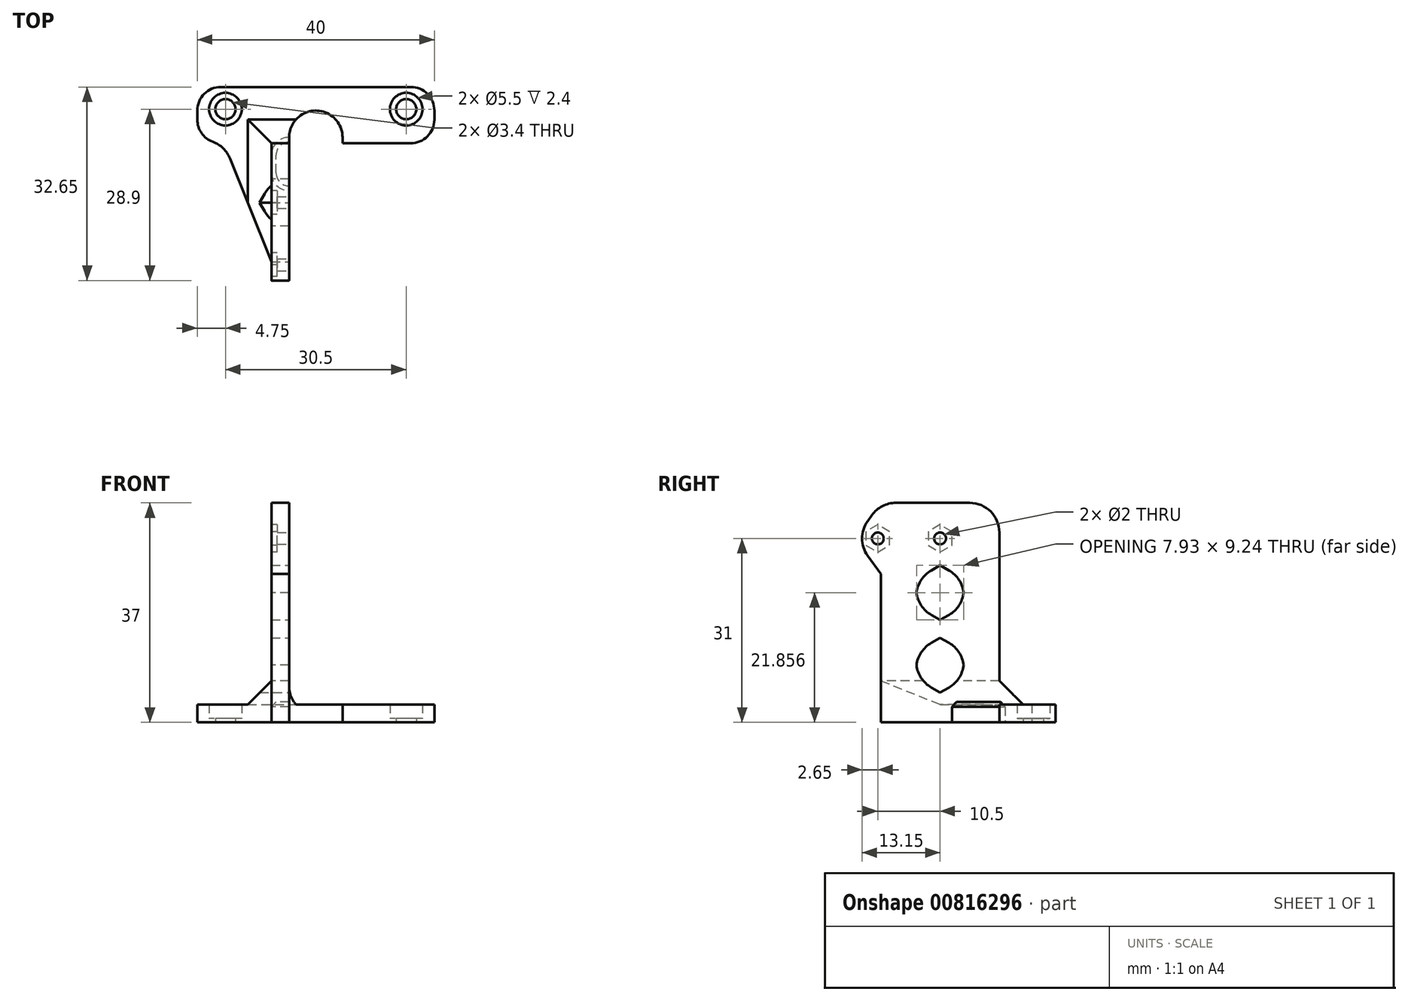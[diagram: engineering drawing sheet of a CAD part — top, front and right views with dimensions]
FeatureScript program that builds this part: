
annotation { "Feature Type Name" : "Feature", "Feature Type Description" : "" }
export const myFeature = defineFeature(function(context is Context, id is Id, definition is map)
    precondition{}
    {
        {
            var Q0;
            Q0=qCreatedBy(makeId("Top.planeOp"),FACE);
            var sketch = newSketch(context, id + "F0", { "sketchPlane" : qUnion([Q0])});
            skLineSegment(sketch, "E0.bottom", {"start": v(-20, 14.75) * mm, "end": v(20, 14.75) * mm});
            skLineSegment(sketch, "E0.top", {"start": v(-20, -14.75) * mm, "end": v(20, -14.75) * mm});
            skLineSegment(sketch, "E0.left", {"start": v(-20, 14.75) * mm, "end": v(-20, -14.75) * mm});
            skLineSegment(sketch, "E0.right", {"start": v(20, 14.75) * mm, "end": v(20, -14.75) * mm});
            skCircle(sketch, "E1", {"center": v(-15.25, 11) * mm, "radius": 2.75 * mm});
            skCircle(sketch, "E2", {"center": v(15.25, 11) * mm, "radius": 2.75 * mm});
            skLineSegment(sketch, "E3", {"start": v(-15.25, 11) * mm, "end": v(15.25, 11) * mm, "construction": true});
            skPoint(sketch, "E4", {"position": v(0, 11) * mm});
            skPoint(sketch, "E5", {"position": v(0, 14.75) * mm});
            skPoint(sketch, "E6", {"position": v(-20, 0) * mm});
            skCircle(sketch, "E7", {"center": v(0, 6.25) * mm, "radius": 4.5 * mm});
            skLineSegment(sketch, "E8", {"start": v(4.5, 6.25) * mm, "end": v(4.5, -14.75) * mm});
            skLineSegment(sketch, "E9", {"start": v(-4.5, 6.25) * mm, "end": v(-4.5, -14.75) * mm});
            skLineSegment(sketch, "E10", {"start": v(-4.5, 5.25) * mm, "end": v(-7.5, 5.25) * mm});
            skLineSegment(sketch, "E11", {"start": v(-7.5, 5.25) * mm, "end": v(-7.5, -14.75) * mm});
            skLineSegment(sketch, "E12", {"start": v(4.5, 5.25) * mm, "end": v(20, 5.25) * mm});
            skLineSegment(sketch, "E13", {"start": v(-7.5, 5.25) * mm, "end": v(-20, 5.25) * mm});
            skCircle(sketch, "E14", {"center": v(-15.25, 11) * mm, "radius": 1.7 * mm});
            skCircle(sketch, "E15", {"center": v(15.25, 11) * mm, "radius": 1.7 * mm});
            skPoint(sketch, "E16", {"position": v(0, 10.75) * mm});
            skPoint(sketch, "E17", {"position": v(15.25, 13.75) * mm});
            skSolve(sketch);
        }
        {
            var Q0;
            {var subQ4=sQuery(id+"F0.wireOp",EDGE,"E10");Q0=makeQuery(id+"F0.imprint","IMPRINT",FACE,{"disambiguationData":[TD([[makeQuery(id+"F0.imprint","IMPRINT",EDGE,{"derivedFrom":subQ4}),1.0]])]});}
            var Q1;
            {var subQ7=sQuery(id+"F0.wireOp",EDGE,"E0.bottom");Q1=makeQuery(id+"F0.imprint","IMPRINT",FACE,{"disambiguationData":[TD([[makeQuery(id+"F0.imprint","IMPRINT",EDGE,{"derivedFrom":subQ7}),-1.0]])]});}
            extrude(context, id + "F1", {"entities" : qUnion([Q0, Q1]), "depth" : 3 * mm, "offsetDistance" : 25 * mm});
        }
        {
            var Q0;
            {var subQ4=sQuery(id+"F0.wireOp",EDGE,"E10");Q0=makeQuery(id+"F0.imprint","IMPRINT",FACE,{"disambiguationData":[TD([[makeQuery(id+"F0.imprint","IMPRINT",EDGE,{"derivedFrom":subQ4}),1.0]])]});}
            extrude(context, id + "F2", {"entities" : qUnion([Q0]), "operationType" : NewBodyOperationType.ADD, "flatOperationType" : FlatOperationType.REMOVE, "depth" : (46 - 9) * mm, "offsetDistance" : 25 * mm, "domain" : OperationDomain.MODEL});
        }
        {
            var Q0;
            Q0=makeQuery(id+"F1.opExtrude","SWEPT_EDGE",EDGE,{"disambiguationData":[OSD([sQuery(id+"F0.wireOp",EDGE,"E0.right"),sQuery(id+"F0.wireOp",EDGE,"E12")])]});
            var Q1;
            Q1=makeQuery(id+"F1.opExtrude","SWEPT_EDGE",EDGE,{"disambiguationData":[OSD([sQuery(id+"F0.wireOp",EDGE,"E0.bottom"),sQuery(id+"F0.wireOp",EDGE,"E0.right")])]});
            var Q2;
            Q2=makeQuery(id+"F1.opExtrude","SWEPT_EDGE",EDGE,{"disambiguationData":[OSD([sQuery(id+"F0.wireOp",EDGE,"E0.left"),sQuery(id+"F0.wireOp",EDGE,"E13")])]});
            var Q3;
            Q3=makeQuery(id+"F1.opExtrude","SWEPT_EDGE",EDGE,{"disambiguationData":[OSD([sQuery(id+"F0.wireOp",EDGE,"E0.bottom"),sQuery(id+"F0.wireOp",EDGE,"E0.left")])]});
            fillet(context, id + "F3", {"entities" : qUnion([Q0, Q1, Q2, Q3]), "radius" : 4 * mm, "tangentPropagation" : true, "allowEdgeOverflow" : false});
        }
        {
            var Q0;
            Q0=makeQuery(id+"F1.opExtrude","SWEPT_EDGE",EDGE,{"disambiguationData":[OSD([sQuery(id+"F0.wireOp",EDGE,"E10"),sQuery(id+"F0.wireOp",EDGE,"E11"),sQuery(id+"F0.wireOp",EDGE,"E13")])]});
            chamfer(context, id + "F4", {"entities" : qUnion([Q0]), "chamferType" : ChamferType.TWO_OFFSETS, "width1" : 20 * mm, "oppositeDirection" : false, "width2" : 8 * mm, "tangentPropagation" : true});
        }
        {
            var Q0;
            {var subQ0=sQuery(id+"F0.wireOp",EDGE,"E13");Q0=makeQuery(id+"F4.opChamfer","BLEND_EDGE",EDGE,{"blendedFrom":[makeQuery(id+"F1.opExtrude","SWEPT_EDGE",EDGE,{"disambiguationData":[OSD([sQuery(id+"F0.wireOp",EDGE,"E10"),sQuery(id+"F0.wireOp",EDGE,"E11"),subQ0])]}),makeQuery(id+"F1.opExtrude","SWEPT_FACE",FACE,{"disambiguationData":[OSD([subQ0])]})],"blendedInto":[makeQuery(id+"F1.opExtrude","SWEPT_FACE",FACE,{"disambiguationData":[OSD([subQ0])]})]});}
            fillet(context, id + "F5", {"entities" : qUnion([Q0]), "radius" : 5 * mm, "tangentPropagation" : true, "allowEdgeOverflow" : false});
        }
        {
            var Q0;
            Q0=makeQuery(id+"F4.opChamfer","TWEAK_EDGE",EDGE,{"derivedFrom":[makeQuery(id+"F1.opExtrude","CAP_VERTEX",VERTEX,{"disambiguationData":[OSD([sQuery(id+"F0.wireOp",EDGE,"E10"),sQuery(id+"F0.wireOp",EDGE,"E11"),sQuery(id+"F0.wireOp",EDGE,"E13")])],"isStart":false})]});
            chamfer(context, id + "F6", {"entities" : qUnion([Q0]), "width" : 4 * mm, "tangentPropagation" : true});
        }
        {
            var Q0;
            {var subQ0=sQuery(id+"F0.wireOp",EDGE,"E9");Q0=makeQuery(id+"F2.boolean.opBoolean","MERGE",FACE,{"derivedFrom":[makeQuery(id+"F1.opExtrude","SWEPT_FACE",FACE,{"disambiguationData":[OSD([subQ0])]}),makeQuery(id+"F2.opExtrude","SWEPT_FACE",FACE,{"disambiguationData":[OSD([subQ0])]})]});}
            var sketch = newSketch(context, id + "F7", { "sketchPlane" : qUnion([Q0])});
            skCircle(sketch, "E18.cCircle", {"center": v(-4.75, 9.62) * mm, "radius": 4 * mm, "construction": true});
            skLineSegment(sketch, "E18.0", {"start": v(-8.75, 7.3) * mm, "end": v(-8.75, 11.93) * mm});
            skLineSegment(sketch, "E18.1", {"start": v(-8.75, 11.93) * mm, "end": v(-4.75, 14.24) * mm});
            skLineSegment(sketch, "E18.2", {"start": v(-4.75, 14.24) * mm, "end": v(-0.75, 11.93) * mm});
            skLineSegment(sketch, "E18.3", {"start": v(-0.75, 11.93) * mm, "end": v(-0.75, 7.3) * mm});
            skLineSegment(sketch, "E18.4", {"start": v(-0.75, 7.3) * mm, "end": v(-4.75, 5) * mm});
            skLineSegment(sketch, "E18.5", {"start": v(-4.75, 5) * mm, "end": v(-8.75, 7.3) * mm});
            skPoint(sketch, "E18.0.midPoint", {"position": v(-8.75, 9.62) * mm});
            skPoint(sketch, "E19", {"position": v(-4.75, 37) * mm});
            skCircle(sketch, "E20", {"center": v(-15.25, 31) * mm, "radius": 1 * mm});
            skCircle(sketch, "E21", {"center": v(-4.75, 31) * mm, "radius": 1 * mm});
            skLineSegment(sketch, "E22", {"start": v(-14.75, 25) * mm, "end": v(-19.05, 31) * mm});
            skLineSegment(sketch, "E23", {"start": v(-19.05, 31) * mm, "end": v(-14.75, 37) * mm});
            skCircle(sketch, "E24.cCircle", {"center": v(-4.75, 21.86) * mm, "radius": 4 * mm, "construction": true});
            skLineSegment(sketch, "E24.0", {"start": v(-8.75, 19.55) * mm, "end": v(-8.75, 24.17) * mm});
            skLineSegment(sketch, "E24.1", {"start": v(-8.75, 24.17) * mm, "end": v(-4.75, 26.48) * mm});
            skLineSegment(sketch, "E24.2", {"start": v(-4.75, 26.48) * mm, "end": v(-0.75, 24.17) * mm});
            skLineSegment(sketch, "E24.3", {"start": v(-0.75, 24.17) * mm, "end": v(-0.75, 19.55) * mm});
            skLineSegment(sketch, "E24.4", {"start": v(-0.75, 19.55) * mm, "end": v(-4.75, 17.24) * mm});
            skLineSegment(sketch, "E24.5", {"start": v(-4.75, 17.24) * mm, "end": v(-8.75, 19.55) * mm});
            skPoint(sketch, "E24.0.midPoint", {"position": v(-8.75, 21.86) * mm});
            skSolve(sketch);
        }
        {
            var Q0;
            Q0=makeQuery(id+"F7.imprint","IMPRINT",FACE,{"disambiguationData":[TD([[makeQuery(id+"F7.imprint","IMPRINT",EDGE,{"derivedFrom":sQuery(id+"F7.wireOp",EDGE,"E24.0")}),-1.0]])]});
            var Q1;
            {var subQ0=sQuery(id+"F7.wireOp",EDGE,"E20");var subQ1=sQuery(id+"F0.wireOp",EDGE,"E9");var subQ2=sQuery(id+"F0.wireOp",EDGE,"E0.top");var subQ3=makeQuery(id+"F2.boolean.opBoolean","MERGE",EDGE,{"derivedFrom":[makeQuery(id+"F1.opExtrude","SWEPT_EDGE",EDGE,{"disambiguationData":[OSD([subQ2,subQ1])]}),makeQuery(id+"F2.opExtrude","SWEPT_EDGE",EDGE,{"disambiguationData":[OSD([subQ2,subQ1])]})]});var subQ4=makeQuery(id+"F7.imprint","INTERSECT",VERTEX,{"disambiguationData":[OD(0.0)],"derivedFrom":[subQ3,subQ0]});Q1=makeQuery(id+"F7.imprint","IMPRINT",FACE,{"disambiguationData":[TD([[makeQuery(id+"F7.imprint","IMPRINT",EDGE,{"disambiguationData":[TD([[subQ4,1.0]])],"derivedFrom":subQ0}),1.0]])]});}
            var Q2;
            Q2=makeQuery(id+"F7.imprint","IMPRINT",FACE,{"disambiguationData":[TD([[makeQuery(id+"F7.imprint","IMPRINT",EDGE,{"derivedFrom":sQuery(id+"F7.wireOp",EDGE,"E18.0")}),-1.0]])]});
            var Q3;
            Q3=makeQuery(id+"F7.imprint","IMPRINT",FACE,{"disambiguationData":[TD([[makeQuery(id+"F7.imprint","IMPRINT",EDGE,{"derivedFrom":sQuery(id+"F7.wireOp",EDGE,"E21")}),1.0]])]});
            extrude(context, id + "F8", {"entities" : qUnion([Q0, Q1, Q2, Q3]), "operationType" : NewBodyOperationType.REMOVE, "oppositeDirection" : true, "depth" : 25 * mm, "offsetDistance" : 25 * mm});
        }
        {
            var Q0;
            {var subQ6=sQuery(id+"F7.wireOp",EDGE,"E22");Q0=makeQuery(id+"F7.imprint","IMPRINT",FACE,{"disambiguationData":[TD([[makeQuery(id+"F7.imprint","IMPRINT",EDGE,{"derivedFrom":subQ6}),-1.0]])]});}
            var Q1;
            {var subQ0=sQuery(id+"F0.wireOp",EDGE,"E11");Q1=makeQuery(id+"F2.boolean.opBoolean","MERGE",FACE,{"derivedFrom":[makeQuery(id+"F1.opExtrude","SWEPT_FACE",FACE,{"disambiguationData":[OSD([subQ0])]}),makeQuery(id+"F2.opExtrude","SWEPT_FACE",FACE,{"disambiguationData":[OSD([subQ0])]})]});}
            extrude(context, id + "F9", {"entities" : qUnion([Q0]), "operationType" : NewBodyOperationType.ADD, "endBound" : BoundingType.UP_TO_SURFACE, "oppositeDirection" : true, "depth" : 25 * mm, "endBoundEntityFace" : qUnion([Q1]), "offsetDistance" : 25 * mm});
        }
        {
            var Q0;
            {var subQ0=sQuery(id+"F0.wireOp",EDGE,"E0.top");Q0=makeQuery(id+"F9.boolean.opBoolean","MERGE",EDGE,{"derivedFrom":[makeQuery(id+"F2.opExtrude","CAP_EDGE",EDGE,{"disambiguationData":[OSD([subQ0])],"isStart":false}),makeQuery(id+"F9.opExtrude","SWEPT_EDGE",EDGE,{"disambiguationData":[OSD([subQ0,sQuery(id+"F0.wireOp",EDGE,"E9"),sQuery(id+"F7.wireOp",EDGE,"E23")])]})]});}
            var Q1;
            Q1=makeQuery(id+"F2.opExtrude","CAP_EDGE",EDGE,{"disambiguationData":[OSD([sQuery(id+"F0.wireOp",EDGE,"E10")])],"isStart":false});
            var Q2;
            Q2=makeQuery(id+"F9.opExtrude","SWEPT_EDGE",EDGE,{"disambiguationData":[OSD([sQuery(id+"F0.wireOp",EDGE,"E0.top"),sQuery(id+"F0.wireOp",EDGE,"E9"),sQuery(id+"F7.wireOp",EDGE,"E22")])]});
            var Q3;
            Q3=makeQuery(id+"F8.boolean.opBoolean","COPY",EDGE,{"derivedFrom":makeQuery(id+"F8.opExtrude","SWEPT_EDGE",EDGE,{"disambiguationData":[OSD([sQuery(id+"F7.wireOp",EDGE,"E24.0"),sQuery(id+"F7.wireOp",EDGE,"E24.1")])]})});
            var Q4;
            Q4=makeQuery(id+"F8.boolean.opBoolean","COPY",EDGE,{"derivedFrom":makeQuery(id+"F8.opExtrude","SWEPT_EDGE",EDGE,{"disambiguationData":[OSD([sQuery(id+"F7.wireOp",EDGE,"E24.2"),sQuery(id+"F7.wireOp",EDGE,"E24.3")])]})});
            var Q5;
            Q5=makeQuery(id+"F8.boolean.opBoolean","COPY",EDGE,{"derivedFrom":makeQuery(id+"F8.opExtrude","SWEPT_EDGE",EDGE,{"disambiguationData":[OSD([sQuery(id+"F7.wireOp",EDGE,"E24.3"),sQuery(id+"F7.wireOp",EDGE,"E24.4")])]})});
            var Q6;
            Q6=makeQuery(id+"F8.boolean.opBoolean","COPY",EDGE,{"derivedFrom":makeQuery(id+"F8.opExtrude","SWEPT_EDGE",EDGE,{"disambiguationData":[OSD([sQuery(id+"F7.wireOp",EDGE,"E24.0"),sQuery(id+"F7.wireOp",EDGE,"E24.5")])]})});
            var Q7;
            Q7=makeQuery(id+"F8.boolean.opBoolean","COPY",EDGE,{"derivedFrom":makeQuery(id+"F8.opExtrude","SWEPT_EDGE",EDGE,{"disambiguationData":[OSD([sQuery(id+"F7.wireOp",EDGE,"E18.0"),sQuery(id+"F7.wireOp",EDGE,"E18.5")])]})});
            var Q8;
            Q8=makeQuery(id+"F8.boolean.opBoolean","COPY",EDGE,{"derivedFrom":makeQuery(id+"F8.opExtrude","SWEPT_EDGE",EDGE,{"disambiguationData":[OSD([sQuery(id+"F7.wireOp",EDGE,"E18.0"),sQuery(id+"F7.wireOp",EDGE,"E18.1")])]})});
            var Q9;
            Q9=makeQuery(id+"F8.boolean.opBoolean","COPY",EDGE,{"derivedFrom":makeQuery(id+"F8.opExtrude","SWEPT_EDGE",EDGE,{"disambiguationData":[OSD([sQuery(id+"F7.wireOp",EDGE,"E18.3"),sQuery(id+"F7.wireOp",EDGE,"E18.4")])]})});
            var Q10;
            Q10=makeQuery(id+"F8.boolean.opBoolean","COPY",EDGE,{"derivedFrom":makeQuery(id+"F8.opExtrude","SWEPT_EDGE",EDGE,{"disambiguationData":[OSD([sQuery(id+"F7.wireOp",EDGE,"E18.2"),sQuery(id+"F7.wireOp",EDGE,"E18.3")])]})});
            var Q11;
            Q11=makeQuery(id+"F9.opExtrude","SWEPT_EDGE",EDGE,{"disambiguationData":[OSD([sQuery(id+"F7.wireOp",EDGE,"E22"),sQuery(id+"F7.wireOp",EDGE,"E23")])]});
            fillet(context, id + "F10", {"entities" : qUnion([Q0, Q1, Q2, Q3, Q4, Q5, Q6, Q7, Q8, Q9, Q10, Q11]), "radius" : 5 * mm, "tangentPropagation" : true, "allowEdgeOverflow" : false});
        }
        {
            var Q0;
            Q0=makeQuery(id+"F0.imprint","IMPRINT",FACE,{"disambiguationData":[TD([[makeQuery(id+"F0.imprint","IMPRINT",EDGE,{"derivedFrom":sQuery(id+"F0.wireOp",EDGE,"E1")}),1.0]])]});
            var Q1;
            Q1=makeQuery(id+"F0.imprint","IMPRINT",FACE,{"disambiguationData":[TD([[makeQuery(id+"F0.imprint","IMPRINT",EDGE,{"derivedFrom":sQuery(id+"F0.wireOp",EDGE,"E2")}),1.0]])]});
            extrude(context, id + "F11", {"entities" : qUnion([Q0, Q1]), "operationType" : NewBodyOperationType.ADD, "depth" : 0.6 * mm, "offsetDistance" : 25 * mm});
        }
        {
            var Q0;
            {var subQ0=sQuery(id+"F0.wireOp",EDGE,"E2");var subQ1=sQuery(id+"F0.wireOp",EDGE,"E1");Q0=makeQuery(id+"F11.boolean.opBoolean","MERGE",FACE,{"derivedFrom":[makeQuery(id+"F1.opExtrude","CAP_FACE",FACE,{"disambiguationData":[OSD([sQuery(id+"F0.wireOp",EDGE,"E0.bottom"),sQuery(id+"F0.wireOp",EDGE,"E0.top"),sQuery(id+"F0.wireOp",EDGE,"E0.left"),sQuery(id+"F0.wireOp",EDGE,"E0.right"),subQ1,subQ0,sQuery(id+"F0.wireOp",EDGE,"E7"),sQuery(id+"F0.wireOp",EDGE,"E8"),sQuery(id+"F0.wireOp",EDGE,"E9"),sQuery(id+"F0.wireOp",EDGE,"E11"),sQuery(id+"F0.wireOp",EDGE,"E12"),sQuery(id+"F0.wireOp",EDGE,"E13")])],"isStart":true}),makeQuery(id+"F11.opExtrude","CAP_FACE",FACE,{"disambiguationData":[OSD([subQ1,sQuery(id+"F0.wireOp",EDGE,"E14")])],"isStart":true}),makeQuery(id+"F11.opExtrude","CAP_FACE",FACE,{"disambiguationData":[OSD([subQ0,sQuery(id+"F0.wireOp",EDGE,"E15")])],"isStart":true})]});}
            var sketch = newSketch(context, id + "F12", { "sketchPlane" : qUnion([Q0])});
            skArc(sketch, "E25", {"start": v(-7.5, -3.25) * mm, "mid": v(-2.38, -5.37) * mm, "end": v(-4.5, -0.25) * mm});
            skArc(sketch, "E26", {"start": v(-4.5, -3.25) * mm, "mid": v(-2.38, 1.87) * mm, "end": v(-7.5, -0.25) * mm});
            skLineSegment(sketch, "E27", {"start": v(-7.5, -3.25) * mm, "end": v(-7.5, 0) * mm});
            skSolve(sketch);
        }
        {
            var Q0;
            Q0=makeQuery(id+"F2.boolean.opBoolean","INTERSECT",EDGE,{"derivedFrom":[makeQuery(id+"F1.opExtrude","CAP_FACE",FACE,{"disambiguationData":[OSD([sQuery(id+"F0.wireOp",EDGE,"E0.bottom"),sQuery(id+"F0.wireOp",EDGE,"E0.top"),sQuery(id+"F0.wireOp",EDGE,"E0.left"),sQuery(id+"F0.wireOp",EDGE,"E0.right"),sQuery(id+"F0.wireOp",EDGE,"E1"),sQuery(id+"F0.wireOp",EDGE,"E2"),sQuery(id+"F0.wireOp",EDGE,"E7"),sQuery(id+"F0.wireOp",EDGE,"E8"),sQuery(id+"F0.wireOp",EDGE,"E9"),sQuery(id+"F0.wireOp",EDGE,"E11"),sQuery(id+"F0.wireOp",EDGE,"E12"),sQuery(id+"F0.wireOp",EDGE,"E13")])],"isStart":false}),makeQuery(id+"F2.opExtrude","SWEPT_FACE",FACE,{"disambiguationData":[OSD([sQuery(id+"F0.wireOp",EDGE,"E10")])]})]});
            chamfer(context, id + "F13", {"entities" : qUnion([Q0]), "width" : 4 * mm, "tangentPropagation" : true});
        }
        {
            var Q0;
            {var subQ3=sQuery(id+"F12.wireOp",EDGE,"E26");var subQ5=sQuery(id+"F12.wireOp",EDGE,"E27");var subQ7=makeQuery(id+"F12.imprint","INTERSECT",VERTEX,{"derivedFrom":[subQ3,subQ5]});Q0=makeQuery(id+"F12.imprint","IMPRINT",FACE,{"disambiguationData":[TD([[makeQuery(id+"F12.imprint","IMPRINT",EDGE,{"disambiguationData":[TD([[subQ7,1.0]])],"derivedFrom":subQ3}),1.0]])]});}
            extrude(context, id + "F14", {"entities" : qUnion([Q0]), "operationType" : NewBodyOperationType.REMOVE, "flatOperationType" : FlatOperationType.REMOVE, "oppositeDirection" : true, "depth" : 3.4 * mm, "offsetDistance" : 25 * mm, "domain" : OperationDomain.MODEL});
        }
        {
            var Q0;
            Q0=makeQuery(id+"F14.boolean.opBoolean","COPY",EDGE,{"derivedFrom":makeQuery(id+"F14.opExtrude","CAP_EDGE",EDGE,{"disambiguationData":[OSD([sQuery(id+"F12.wireOp",EDGE,"E27")])],"isStart":false})});
            var Q1;
            Q1=makeQuery(id+"F14.boolean.opBoolean","COPY",EDGE,{"derivedFrom":makeQuery(id+"F14.opExtrude","CAP_EDGE",EDGE,{"disambiguationData":[OSD([sQuery(id+"F12.wireOp",EDGE,"E25")])],"isStart":false})});
            var Q2;
            Q2=makeQuery(id+"F14.boolean.opBoolean","COPY",EDGE,{"derivedFrom":makeQuery(id+"F14.opExtrude","CAP_EDGE",EDGE,{"disambiguationData":[OSD([sQuery(id+"F12.wireOp",EDGE,"E26")])],"isStart":false})});
            chamfer(context, id + "F15", {"entities" : qUnion([Q0, Q1, Q2]), "width" : 0.8 * mm});
        }
        {
            var Q0;
            {var subQ0=sQuery(id+"F0.wireOp",EDGE,"E11");Q0=makeQuery(id+"F9.boolean.opBoolean","MERGE",FACE,{"derivedFrom":[makeQuery(id+"F2.boolean.opBoolean","MERGE",FACE,{"derivedFrom":[makeQuery(id+"F1.opExtrude","SWEPT_FACE",FACE,{"disambiguationData":[OSD([subQ0])]}),makeQuery(id+"F2.opExtrude","SWEPT_FACE",FACE,{"disambiguationData":[OSD([subQ0])]})]}),makeQuery(id+"F9.opExtrude","CAP_FACE",FACE,{"disambiguationData":[OSD([sQuery(id+"F0.wireOp",EDGE,"E0.top"),sQuery(id+"F0.wireOp",EDGE,"E9"),sQuery(id+"F7.wireOp",EDGE,"E20"),sQuery(id+"F7.wireOp",EDGE,"E22"),sQuery(id+"F7.wireOp",EDGE,"E23")])],"isStart":false})]});}
            var sketch = newSketch(context, id + "F16", { "sketchPlane" : qUnion([Q0])});
            skCircle(sketch, "E28.cCircle", {"center": v(4.75, 31) * mm, "radius": 2 * mm, "construction": true});
            skLineSegment(sketch, "E28.0", {"start": v(6.75, 32.15) * mm, "end": v(6.75, 29.85) * mm});
            skLineSegment(sketch, "E28.1", {"start": v(6.75, 29.85) * mm, "end": v(4.75, 28.7) * mm});
            skLineSegment(sketch, "E28.2", {"start": v(4.75, 28.7) * mm, "end": v(2.75, 29.85) * mm});
            skLineSegment(sketch, "E28.3", {"start": v(2.75, 29.85) * mm, "end": v(2.75, 32.15) * mm});
            skLineSegment(sketch, "E28.4", {"start": v(2.75, 32.15) * mm, "end": v(4.75, 33.3) * mm});
            skLineSegment(sketch, "E28.5", {"start": v(4.75, 33.3) * mm, "end": v(6.75, 32.15) * mm});
            skPoint(sketch, "E28.0.midPoint", {"position": v(6.75, 31) * mm});
            skCircle(sketch, "E29.cCircle", {"center": v(15.25, 31) * mm, "radius": 2 * mm, "construction": true});
            skLineSegment(sketch, "E29.0", {"start": v(13.25, 29.85) * mm, "end": v(13.25, 32.15) * mm});
            skLineSegment(sketch, "E29.1", {"start": v(13.25, 32.15) * mm, "end": v(15.25, 33.3) * mm});
            skLineSegment(sketch, "E29.2", {"start": v(15.25, 33.3) * mm, "end": v(17.25, 32.15) * mm});
            skLineSegment(sketch, "E29.3", {"start": v(17.25, 32.15) * mm, "end": v(17.25, 29.85) * mm});
            skLineSegment(sketch, "E29.4", {"start": v(17.25, 29.85) * mm, "end": v(15.25, 28.7) * mm});
            skLineSegment(sketch, "E29.5", {"start": v(15.25, 28.7) * mm, "end": v(13.25, 29.85) * mm});
            skPoint(sketch, "E29.0.midPoint", {"position": v(13.25, 31) * mm});
            skSolve(sketch);
        }
        {
            var Q0;
            Q0=makeQuery(id+"F16.imprint","IMPRINT",FACE,{"disambiguationData":[TD([[makeQuery(id+"F16.imprint","IMPRINT",EDGE,{"derivedFrom":sQuery(id+"F16.wireOp",EDGE,"E28.0")}),-1.0]])]});
            var Q1;
            Q1=makeQuery(id+"F16.imprint","IMPRINT",FACE,{"disambiguationData":[TD([[makeQuery(id+"F16.imprint","IMPRINT",EDGE,{"derivedFrom":sQuery(id+"F16.wireOp",EDGE,"E29.0")}),-1.0]])]});
            extrude(context, id + "F17", {"entities" : qUnion([Q0, Q1]), "operationType" : NewBodyOperationType.REMOVE, "oppositeDirection" : true, "depth" : 1 * mm, "offsetDistance" : 25 * mm});
        }
    });
